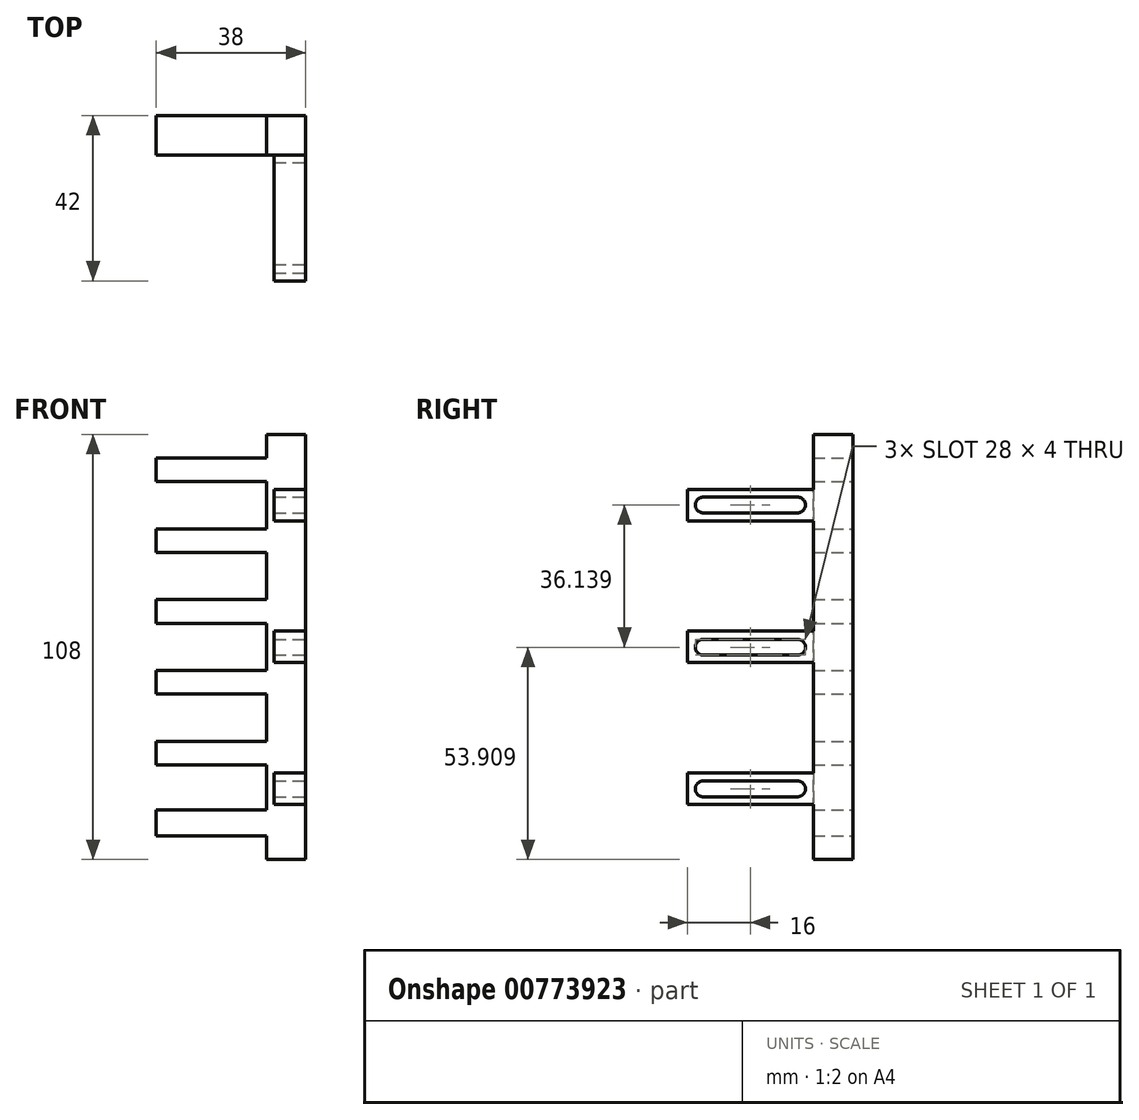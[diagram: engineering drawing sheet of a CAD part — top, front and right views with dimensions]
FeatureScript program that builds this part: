
annotation { "Feature Type Name" : "Feature", "Feature Type Description" : "" }
export const myFeature = defineFeature(function(context is Context, id is Id, definition is map)
    precondition{}
    {
        {
            var Q0;
            Q0=qCreatedBy(makeId("Front.planeOp"),FACE);
            var sketch = newSketch(context, id + "F0", { "sketchPlane" : qUnion([Q0])});
            skLineSegment(sketch, "E0.bottom", {"start": v(-38, 50.99) * mm, "end": v(0, 50.99) * mm});
            skLineSegment(sketch, "E0.top", {"start": v(-38, -57.01) * mm, "end": v(0, -57.01) * mm});
            skLineSegment(sketch, "E0.left", {"start": v(-38, 50.99) * mm, "end": v(-38, -57.01) * mm});
            skLineSegment(sketch, "E0.right", {"start": v(0, 50.99) * mm, "end": v(0, -57.01) * mm});
            skSolve(sketch);
        }
        {
            var Q0;
            Q0 = qSketchRegion(id + "F0", true);
            extrude(context, id + "F1", {"entities" : qUnion([Q0]), "depth" : 10 * mm, "offsetDistance" : 25 * mm});
        }
        {
            var Q0;
            Q0=makeQuery(id+"F1.opExtrude","CAP_FACE",FACE,{"disambiguationData":[OSD([sQuery(id+"F0.wireOp",EDGE,"E0.bottom"),sQuery(id+"F0.wireOp",EDGE,"E0.top"),sQuery(id+"F0.wireOp",EDGE,"E0.left"),sQuery(id+"F0.wireOp",EDGE,"E0.right")])],"isStart":false});
            var sketch = newSketch(context, id + "F2", { "sketchPlane" : qUnion([Q0])});
            skLineSegment(sketch, "E1.bottom", {"start": v(-8, 36.99) * mm, "end": v(0, 36.99) * mm});
            skLineSegment(sketch, "E1.top", {"start": v(-8, 28.99) * mm, "end": v(0, 28.99) * mm});
            skLineSegment(sketch, "E1.left", {"start": v(-8, 36.99) * mm, "end": v(-8, 28.99) * mm});
            skLineSegment(sketch, "E1.right", {"start": v(0, 36.99) * mm, "end": v(0, 28.99) * mm});
            skLineSegment(sketch, "E2.bottom", {"start": v(-8, 0.99) * mm, "end": v(0, 0.99) * mm});
            skLineSegment(sketch, "E2.top", {"start": v(-8, -7.01) * mm, "end": v(0, -7.01) * mm});
            skLineSegment(sketch, "E2.left", {"start": v(-8, 0.99) * mm, "end": v(-8, -7.01) * mm});
            skLineSegment(sketch, "E2.right", {"start": v(0, 0.99) * mm, "end": v(0, -7.01) * mm});
            skLineSegment(sketch, "E3.bottom", {"start": v(-8, -35.01) * mm, "end": v(0, -35.01) * mm});
            skLineSegment(sketch, "E3.top", {"start": v(-8, -43.01) * mm, "end": v(0, -43.01) * mm});
            skLineSegment(sketch, "E3.left", {"start": v(-8, -35.01) * mm, "end": v(-8, -43.01) * mm});
            skLineSegment(sketch, "E3.right", {"start": v(0, -35.01) * mm, "end": v(0, -43.01) * mm});
            skSolve(sketch);
        }
        {
            var Q0;
            Q0 = qSketchRegion(id + "F2", true);
            extrude(context, id + "F3", {"entities" : qUnion([Q0]), "operationType" : NewBodyOperationType.ADD, "depth" : 32 * mm, "offsetDistance" : 25 * mm});
        }
        {
            var Q0;
            Q0=makeQuery(id+"F1.opExtrude","CAP_FACE",FACE,{"disambiguationData":[OSD([sQuery(id+"F0.wireOp",EDGE,"E0.bottom"),sQuery(id+"F0.wireOp",EDGE,"E0.top"),sQuery(id+"F0.wireOp",EDGE,"E0.left"),sQuery(id+"F0.wireOp",EDGE,"E0.right")])],"isStart":true});
            var sketch = newSketch(context, id + "F4", { "sketchPlane" : qUnion([Q0])});
            skLineSegment(sketch, "E4.bottom", {"start": v(0, 44.99) * mm, "end": v(38, 44.99) * mm});
            skLineSegment(sketch, "E4.top", {"start": v(0, 50.99) * mm, "end": v(38, 50.99) * mm});
            skLineSegment(sketch, "E4.left", {"start": v(0, 44.99) * mm, "end": v(0, 50.99) * mm});
            skLineSegment(sketch, "E4.right", {"start": v(38, 44.99) * mm, "end": v(38, 50.99) * mm});
            skSolve(sketch);
        }
        {
            var Q0;
            Q0 = qSketchRegion(id + "F4", true);
            extrude(context, id + "F5", {"entities" : qUnion([Q0]), "operationType" : NewBodyOperationType.REMOVE, "oppositeDirection" : true, "depth" : 25 * mm, "offsetDistance" : 25 * mm});
        }
        {
            var Q0;
            Q0=makeQuery(id+"F1.opExtrude","CAP_FACE",FACE,{"disambiguationData":[OSD([sQuery(id+"F0.wireOp",EDGE,"E0.bottom"),sQuery(id+"F0.wireOp",EDGE,"E0.top"),sQuery(id+"F0.wireOp",EDGE,"E0.left"),sQuery(id+"F0.wireOp",EDGE,"E0.right")])],"isStart":true});
            var sketch = newSketch(context, id + "F6", { "sketchPlane" : qUnion([Q0])});
            skLineSegment(sketch, "E5.bottom", {"start": v(10, 38.99) * mm, "end": v(38, 38.99) * mm});
            skLineSegment(sketch, "E5.top", {"start": v(10, 26.99) * mm, "end": v(38, 26.99) * mm});
            skLineSegment(sketch, "E5.left", {"start": v(10, 38.99) * mm, "end": v(10, 26.99) * mm});
            skLineSegment(sketch, "E5.right", {"start": v(38, 38.99) * mm, "end": v(38, 26.99) * mm});
            skLineSegment(sketch, "E6.bottom", {"start": v(10, 20.99) * mm, "end": v(38, 20.99) * mm});
            skLineSegment(sketch, "E6.top", {"start": v(10, 8.99) * mm, "end": v(38, 8.99) * mm});
            skLineSegment(sketch, "E6.left", {"start": v(10, 20.99) * mm, "end": v(10, 8.99) * mm});
            skLineSegment(sketch, "E6.right", {"start": v(38, 20.99) * mm, "end": v(38, 8.99) * mm});
            skLineSegment(sketch, "E7.bottom", {"start": v(10, 2.99) * mm, "end": v(38, 2.99) * mm});
            skLineSegment(sketch, "E7.top", {"start": v(10, -9.01) * mm, "end": v(38, -9.01) * mm});
            skLineSegment(sketch, "E7.left", {"start": v(10, 2.99) * mm, "end": v(10, -9.01) * mm});
            skLineSegment(sketch, "E7.right", {"start": v(38, 2.99) * mm, "end": v(38, -9.01) * mm});
            skLineSegment(sketch, "E8.bottom", {"start": v(10, -15.01) * mm, "end": v(38, -15.01) * mm});
            skLineSegment(sketch, "E8.top", {"start": v(10, -27.01) * mm, "end": v(38, -27.01) * mm});
            skLineSegment(sketch, "E8.left", {"start": v(10, -15.01) * mm, "end": v(10, -27.01) * mm});
            skLineSegment(sketch, "E8.right", {"start": v(38, -15.01) * mm, "end": v(38, -27.01) * mm});
            skLineSegment(sketch, "E9.bottom", {"start": v(10, -33.01) * mm, "end": v(38, -33.01) * mm});
            skLineSegment(sketch, "E9.top", {"start": v(10, -44.45) * mm, "end": v(38, -44.45) * mm});
            skLineSegment(sketch, "E9.left", {"start": v(10, -33.01) * mm, "end": v(10, -44.45) * mm});
            skLineSegment(sketch, "E9.right", {"start": v(38, -33.01) * mm, "end": v(38, -44.45) * mm});
            skLineSegment(sketch, "E10.bottom", {"start": v(0, -57.01) * mm, "end": v(38, -57.01) * mm});
            skLineSegment(sketch, "E10.top", {"start": v(0, -51.01) * mm, "end": v(38, -51.01) * mm});
            skLineSegment(sketch, "E10.left", {"start": v(0, -57.01) * mm, "end": v(0, -51.01) * mm});
            skLineSegment(sketch, "E10.right", {"start": v(38, -57.01) * mm, "end": v(38, -51.01) * mm});
            skSolve(sketch);
        }
        {
            var Q0;
            Q0 = qSketchRegion(id + "F6", true);
            extrude(context, id + "F7", {"entities" : qUnion([Q0]), "operationType" : NewBodyOperationType.REMOVE, "oppositeDirection" : true, "depth" : 25 * mm, "offsetDistance" : 25 * mm});
        }
        {
            var Q0;
            Q0 = qSketchRegion(id + "F6", true);
            extrude(context, id + "F8", {"entities" : qUnion([Q0]), "operationType" : NewBodyOperationType.REMOVE, "oppositeDirection" : true, "depth" : 25 * mm, "offsetDistance" : 25 * mm});
        }
        {
            var Q0;
            Q0=makeQuery(id+"F5.boolean.opBoolean","COPY",FACE,{"derivedFrom":makeQuery(id+"F5.opExtrude","SWEPT_FACE",FACE,{"disambiguationData":[OSD([sQuery(id+"F4.wireOp",EDGE,"E4.bottom")])]})});
            var sketch = newSketch(context, id + "F9", { "sketchPlane" : qUnion([Q0])});
            skLineSegment(sketch, "E11.bottom", {"start": v(0, -10) * mm, "end": v(-10, -10) * mm});
            skLineSegment(sketch, "E11.top", {"start": v(0, 0) * mm, "end": v(-10, 0) * mm});
            skLineSegment(sketch, "E11.left", {"start": v(0, -10) * mm, "end": v(0, 0) * mm});
            skLineSegment(sketch, "E11.right", {"start": v(-10, -10) * mm, "end": v(-10, 0) * mm});
            skSolve(sketch);
        }
        {
            var Q0;
            Q0 = qSketchRegion(id + "F9", true);
            extrude(context, id + "F10", {"entities" : qUnion([Q0]), "operationType" : NewBodyOperationType.ADD, "depth" : 6 * mm, "offsetDistance" : 25 * mm});
        }
        {
            var Q0;
            Q0=makeQuery(id+"F7.boolean.opBoolean","COPY",FACE,{"derivedFrom":makeQuery(id+"F7.opExtrude","SWEPT_FACE",FACE,{"disambiguationData":[OSD([sQuery(id+"F6.wireOp",EDGE,"E10.top")])]})});
            var sketch = newSketch(context, id + "F11", { "sketchPlane" : qUnion([Q0])});
            skLineSegment(sketch, "E12.bottom", {"start": v(0, 10) * mm, "end": v(-10, 10) * mm});
            skLineSegment(sketch, "E12.top", {"start": v(0, 0) * mm, "end": v(-10, 0) * mm});
            skLineSegment(sketch, "E12.left", {"start": v(0, 10) * mm, "end": v(0, 0) * mm});
            skLineSegment(sketch, "E12.right", {"start": v(-10, 10) * mm, "end": v(-10, 0) * mm});
            skSolve(sketch);
        }
        {
            var Q0;
            Q0 = qSketchRegion(id + "F11", true);
            extrude(context, id + "F12", {"entities" : qUnion([Q0]), "operationType" : NewBodyOperationType.ADD, "depth" : 6 * mm, "offsetDistance" : 25 * mm});
        }
        {
            var Q0;
            Q0=makeQuery(id+"F12.boolean.opBoolean","MERGE",FACE,{"derivedFrom":[makeQuery(id+"F10.boolean.opBoolean","MERGE",FACE,{"derivedFrom":[makeQuery(id+"F3.boolean.opBoolean","MERGE",FACE,{"derivedFrom":[makeQuery(id+"F1.opExtrude","SWEPT_FACE",FACE,{"disambiguationData":[OSD([sQuery(id+"F0.wireOp",EDGE,"E0.right")])]}),makeQuery(id+"F3.opExtrude","SWEPT_FACE",FACE,{"disambiguationData":[OSD([sQuery(id+"F2.wireOp",EDGE,"E1.right")])]}),makeQuery(id+"F3.opExtrude","SWEPT_FACE",FACE,{"disambiguationData":[OSD([sQuery(id+"F2.wireOp",EDGE,"E2.right")])]}),makeQuery(id+"F3.opExtrude","SWEPT_FACE",FACE,{"disambiguationData":[OSD([sQuery(id+"F2.wireOp",EDGE,"E3.right")])]})]}),makeQuery(id+"F10.opExtrude","SWEPT_FACE",FACE,{"disambiguationData":[OSD([sQuery(id+"F9.wireOp",EDGE,"E11.left")])]})]}),makeQuery(id+"F12.opExtrude","SWEPT_FACE",FACE,{"disambiguationData":[OSD([sQuery(id+"F11.wireOp",EDGE,"E12.left")])]})]});
            var sketch = newSketch(context, id + "F13", { "sketchPlane" : qUnion([Q0])});
            skCircle(sketch, "E13", {"center": v(-38, 33.04) * mm, "radius": 2 * mm});
            skCircle(sketch, "E14", {"center": v(-38, -3.1) * mm, "radius": 2 * mm});
            skCircle(sketch, "E15", {"center": v(-38, -39.1) * mm, "radius": 2 * mm});
            skCircle(sketch, "E16", {"center": v(-14, 33.04) * mm, "radius": 2 * mm});
            skLineSegment(sketch, "E17", {"start": v(-38, 35.04) * mm, "end": v(-14, 35.04) * mm});
            skLineSegment(sketch, "E18", {"start": v(-38, 31.04) * mm, "end": v(-14, 31.04) * mm});
            skCircle(sketch, "E19", {"center": v(-14, -3.1) * mm, "radius": 2 * mm});
            skCircle(sketch, "E20", {"center": v(-14, -39.1) * mm, "radius": 2 * mm});
            skLineSegment(sketch, "E21", {"start": v(-38.07, -1.1) * mm, "end": v(-14, -1.1) * mm});
            skLineSegment(sketch, "E22", {"start": v(-37.9, -5.1) * mm, "end": v(-14, -5.1) * mm});
            skLineSegment(sketch, "E23", {"start": v(-38.01, -37.1) * mm, "end": v(-14, -37.1) * mm});
            skLineSegment(sketch, "E24", {"start": v(-38.14, -41.1) * mm, "end": v(-14, -41.1) * mm});
            skSolve(sketch);
        }
        {
            var Q0;
            Q0 = qSketchRegion(id + "F13", true);
            extrude(context, id + "F14", {"entities" : qUnion([Q0]), "operationType" : NewBodyOperationType.REMOVE, "oppositeDirection" : true, "depth" : 25 * mm, "offsetDistance" : 25 * mm});
        }
        {
            var Q0;
            Q0 = qSketchRegion(id + "F13", true);
            extrude(context, id + "F15", {"entities" : qUnion([Q0]), "operationType" : NewBodyOperationType.REMOVE, "oppositeDirection" : true, "depth" : 25 * mm, "offsetDistance" : 25 * mm});
        }
    });
